# Revit family: РИДАН_Регулятор давления_ДО СЕБЯ_C301R
name_source: partatom
category: Арматура трубопроводов
units: mm (PartAtom-declared; Revit-internal decimal feet)

## family parameters
Всегда вертикально = Да
На основе рабочей плоскости = Нет
Общий = Нет
При загрузке вырезать с полостями = Нет
Размер круглого соединителя = Использовать диаметр
Тип детали = Вставляется

## types (1)
- DN150
    ADSK_Версия Revit = 2019
    ADSK_Версия семейства = 1.0
    ADSK_Диаметр условный = 150 мм
    ADSK_Единица измерения = шт.
    ADSK_Завод-изготовитель = ООО «Ридан-Трейд»
    ADSK_Код изделия = 082X6145RL
    ADSK_Количество = 1
    ADSK_Марка = C301-R DN150 (1-8)
    ADSK_Масса = 0
    ADSK_Материал = <По категории>
    ADSK_Наименование = Регулятор давления «до себя» С301-R PN16, Tmax=150C, DN150 (1-8 бар)
    URL = https://ridan.ru
    a = 18 мм
    a1 = 168 мм
    b = 407 мм
    d = 193 мм
    e = 167 мм
    f = 91 мм
    g = 203 мм
    i = 32 мм
    j = 480 мм
    УГО_Длина = 480 мм
